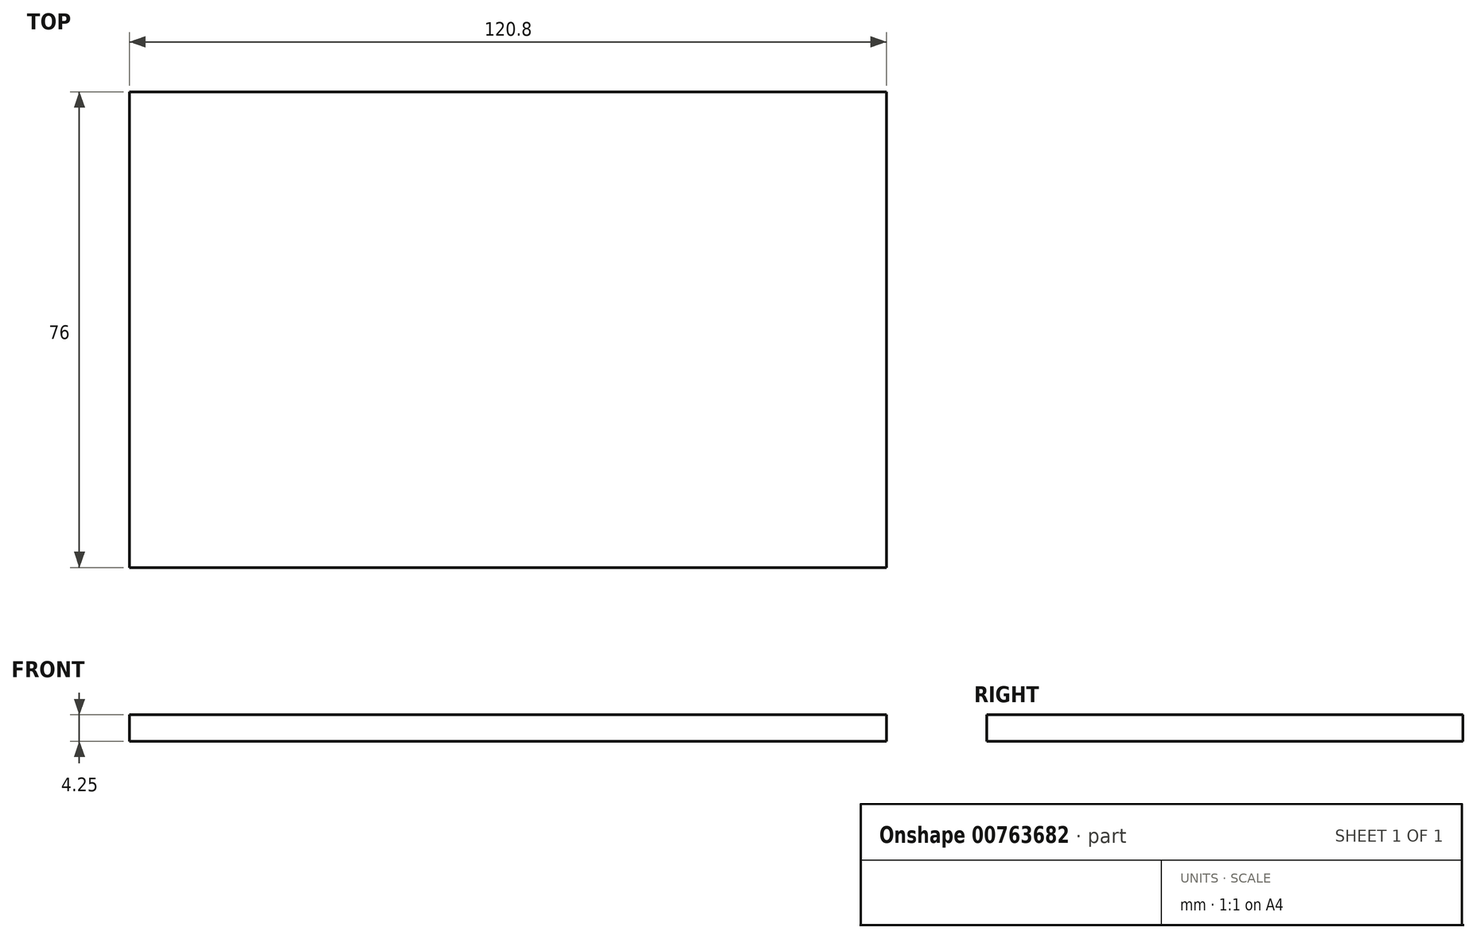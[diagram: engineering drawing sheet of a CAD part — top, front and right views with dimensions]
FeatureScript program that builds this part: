
annotation { "Feature Type Name" : "Feature", "Feature Type Description" : "" }
export const myFeature = defineFeature(function(context is Context, id is Id, definition is map)
    precondition{}
    {
        {
            var Q0;
            Q0=qCreatedBy(makeId("Top.planeOp"),FACE);
            var sketch = newSketch(context, id + "F0", { "sketchPlane" : qUnion([Q0])});
            skLineSegment(sketch, "E0.bottom", {"start": v(60.4, -38) * mm, "end": v(-60.4, -38) * mm});
            skLineSegment(sketch, "E0.top", {"start": v(60.4, 38) * mm, "end": v(-60.4, 38) * mm});
            skLineSegment(sketch, "E0.left", {"start": v(60.4, -38) * mm, "end": v(60.4, 38) * mm});
            skLineSegment(sketch, "E0.right", {"start": v(-60.4, -38) * mm, "end": v(-60.4, 38) * mm});
            skPoint(sketch, "E0.middle", {"position": v(0, 0) * mm});
            skSolve(sketch);
        }
        {
            var Q0;
            Q0=makeQuery(id+"F0.imprint","IMPRINT",FACE,{"disambiguationData":[TD([[makeQuery(id+"F0.imprint","IMPRINT",EDGE,{"derivedFrom":sQuery(id+"F0.wireOp",EDGE,"E0.bottom")}),-1.0]])]});
            extrude(context, id + "F1", {"entities" : qUnion([Q0]), "depth" : 4.25 * mm, "offsetDistance" : 25 * mm});
        }
    });
